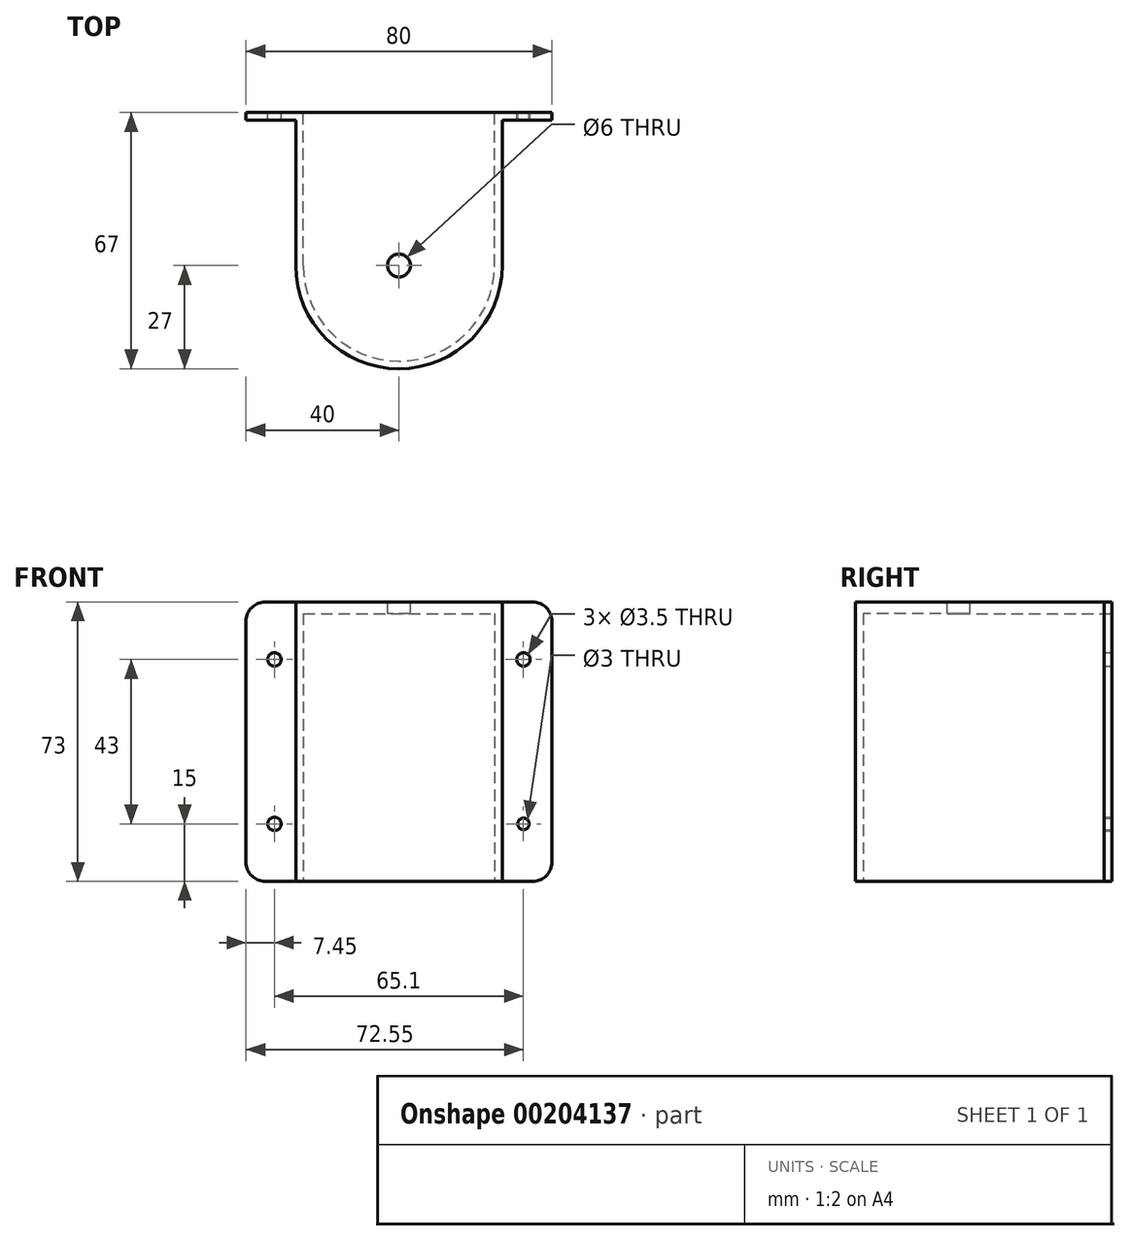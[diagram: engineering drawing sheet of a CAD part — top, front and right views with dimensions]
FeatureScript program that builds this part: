
annotation { "Feature Type Name" : "Feature", "Feature Type Description" : "" }
export const myFeature = defineFeature(function(context is Context, id is Id, definition is map)
    precondition{}
    {
        {
            var Q0;
            Q0=qCreatedBy(makeId("Top.planeOp"),FACE);
            var sketch = newSketch(context, id + "F0", { "sketchPlane" : qUnion([Q0])});
            skLineSegment(sketch, "E0", {"start": v(-25, 0) * mm, "end": v(25, 0) * mm, "construction": true});
            skArc(sketch, "E1", {"start": v(-25, 0) * mm, "mid": v(0, -25) * mm, "end": v(25, 0) * mm});
            skLineSegment(sketch, "E2", {"start": v(-25, 0) * mm, "end": v(-25, 40) * mm});
            skLineSegment(sketch, "E3", {"start": v(25, 0) * mm, "end": v(25, 40) * mm});
            skLineSegment(sketch, "E4", {"start": v(25, 40) * mm, "end": v(40, 40) * mm});
            skLineSegment(sketch, "E5", {"start": v(40, 40) * mm, "end": v(40, 38) * mm});
            skLineSegment(sketch, "E6", {"start": v(40, 38) * mm, "end": v(27, 38) * mm});
            skLineSegment(sketch, "E7", {"start": v(27, 38) * mm, "end": v(27, 0) * mm});
            skLineSegment(sketch, "E8", {"start": v(-25, 40) * mm, "end": v(-40, 40) * mm});
            skLineSegment(sketch, "E9", {"start": v(-40, 40) * mm, "end": v(-40, 38) * mm});
            skLineSegment(sketch, "E10", {"start": v(-40, 38) * mm, "end": v(-27, 38) * mm});
            skLineSegment(sketch, "E11", {"start": v(-27, 38) * mm, "end": v(-27, 0) * mm});
            skArc(sketch, "E12", {"start": v(-27, 0) * mm, "mid": v(0, -27) * mm, "end": v(27, 0) * mm});
            skSolve(sketch);
        }
        {
            var Q0;
            Q0=makeQuery(id+"F0.imprint","IMPRINT",FACE,{"disambiguationData":[TD([[makeQuery(id+"F0.imprint","IMPRINT",EDGE,{"derivedFrom":sQuery(id+"F0.wireOp",EDGE,"E1")}),-1.0]])]});
            extrude(context, id + "F1", {"entities" : qUnion([Q0]), "depth" : 70 * mm});
        }
        {
            var Q0;
            Q0=makeQuery(id+"F1.opExtrude","CAP_FACE",FACE,{"disambiguationData":[OSD([sQuery(id+"F0.wireOp",EDGE,"E1"),sQuery(id+"F0.wireOp",EDGE,"E2"),sQuery(id+"F0.wireOp",EDGE,"E3"),sQuery(id+"F0.wireOp",EDGE,"E4"),sQuery(id+"F0.wireOp",EDGE,"E5"),sQuery(id+"F0.wireOp",EDGE,"E6"),sQuery(id+"F0.wireOp",EDGE,"E7"),sQuery(id+"F0.wireOp",EDGE,"E8"),sQuery(id+"F0.wireOp",EDGE,"E9"),sQuery(id+"F0.wireOp",EDGE,"E10"),sQuery(id+"F0.wireOp",EDGE,"E11"),sQuery(id+"F0.wireOp",EDGE,"E12")])],"isStart":false});
            var sketch = newSketch(context, id + "F2", { "sketchPlane" : qUnion([Q0])});
            skLineSegment(sketch, "E13", {"start": v(-40, 40) * mm, "end": v(40, 40) * mm});
            skLineSegment(sketch, "E14", {"start": v(40, 40) * mm, "end": v(40, 38) * mm});
            skLineSegment(sketch, "E15", {"start": v(40, 38) * mm, "end": v(27, 38) * mm});
            skLineSegment(sketch, "E16", {"start": v(27, 38) * mm, "end": v(27, 0) * mm});
            skLineSegment(sketch, "E17", {"start": v(-40, 40) * mm, "end": v(-40, 38) * mm});
            skLineSegment(sketch, "E18", {"start": v(-40, 38) * mm, "end": v(-27, 38) * mm});
            skLineSegment(sketch, "E19", {"start": v(-27, 38) * mm, "end": v(-27, 0) * mm});
            skArc(sketch, "E20", {"start": v(-27, 0) * mm, "mid": v(0, -27) * mm, "end": v(27, 0) * mm});
            skSolve(sketch);
        }
        {
            var Q0;
            Q0 = qSketchRegion(id + "F2", true);
            extrude(context, id + "F3", {"entities" : qUnion([Q0]), "operationType" : NewBodyOperationType.ADD, "depth" : 3 * mm});
        }
        {
            var Q0;
            Q0=makeQuery(id+"F3.opExtrude","CAP_FACE",FACE,{"disambiguationData":[OSD([sQuery(id+"F2.wireOp",EDGE,"E13"),sQuery(id+"F2.wireOp",EDGE,"E14"),sQuery(id+"F2.wireOp",EDGE,"E15"),sQuery(id+"F2.wireOp",EDGE,"E16"),sQuery(id+"F2.wireOp",EDGE,"E17"),sQuery(id+"F2.wireOp",EDGE,"E18"),sQuery(id+"F2.wireOp",EDGE,"E19"),sQuery(id+"F2.wireOp",EDGE,"E20")])],"isStart":false});
            var sketch = newSketch(context, id + "F4", { "sketchPlane" : qUnion([Q0])});
            skCircle(sketch, "E21", {"center": v(0, 0) * mm, "radius": 3 * mm});
            skSolve(sketch);
        }
        {
            var Q0;
            Q0 = qSketchRegion(id + "F4", true);
            extrude(context, id + "F5", {"entities" : qUnion([Q0]), "operationType" : NewBodyOperationType.REMOVE, "endBound" : BoundingType.UP_TO_NEXT, "oppositeDirection" : true, "depth" : 3 * mm});
        }
        {
            var Q0;
            Q0=makeQuery(id+"F1.opExtrude","CAP_EDGE",EDGE,{"disambiguationData":[OSD([sQuery(id+"F0.wireOp",EDGE,"E5")])],"isStart":true});
            fillet(context, id + "F6", {"entities" : qUnion([Q0]), "radius" : 5 * mm, "tangentPropagation" : true, "allowEdgeOverflow" : false});
        }
        {
            var Q0;
            Q0=makeQuery(id+"F1.opExtrude","CAP_EDGE",EDGE,{"disambiguationData":[OSD([sQuery(id+"F0.wireOp",EDGE,"E9")])],"isStart":true});
            fillet(context, id + "F7", {"entities" : qUnion([Q0]), "radius" : 5 * mm, "tangentPropagation" : true, "allowEdgeOverflow" : false});
        }
        {
            var Q0;
            Q0=makeQuery(id+"F3.opExtrude","CAP_EDGE",EDGE,{"disambiguationData":[OSD([sQuery(id+"F2.wireOp",EDGE,"E17")])],"isStart":false});
            fillet(context, id + "F8", {"entities" : qUnion([Q0]), "radius" : 5 * mm, "tangentPropagation" : true, "allowEdgeOverflow" : false});
        }
        {
            var Q0;
            Q0=makeQuery(id+"F3.opExtrude","CAP_EDGE",EDGE,{"disambiguationData":[OSD([sQuery(id+"F2.wireOp",EDGE,"E14")])],"isStart":false});
            fillet(context, id + "F9", {"entities" : qUnion([Q0]), "radius" : 5 * mm, "tangentPropagation" : true, "allowEdgeOverflow" : false});
        }
        {
            var Q0;
            Q0=makeQuery(id+"F3.boolean.opBoolean","MERGE",FACE,{"derivedFrom":[makeQuery(id+"F1.opExtrude","SWEPT_FACE",FACE,{"disambiguationData":[OSD([sQuery(id+"F0.wireOp",EDGE,"E4")])]}),makeQuery(id+"F1.opExtrude","SWEPT_FACE",FACE,{"disambiguationData":[OSD([sQuery(id+"F0.wireOp",EDGE,"E8")])]}),makeQuery(id+"F3.opExtrude","SWEPT_FACE",FACE,{"disambiguationData":[OSD([sQuery(id+"F2.wireOp",EDGE,"E13")])]})]});
            var sketch = newSketch(context, id + "F10", { "sketchPlane" : qUnion([Q0])});
            skCircle(sketch, "E22", {"center": v(-32.55, 58) * mm, "radius": 1.75 * mm});
            skCircle(sketch, "E23", {"center": v(-32.55, 15) * mm, "radius": 1.5 * mm});
            skCircle(sketch, "E24", {"center": v(32.55, 15) * mm, "radius": 1.75 * mm});
            skCircle(sketch, "E25", {"center": v(32.55, 58) * mm, "radius": 1.75 * mm});
            skSolve(sketch);
        }
        {
            var Q0;
            Q0=makeQuery(id+"F10.imprint","IMPRINT",FACE,{"disambiguationData":[TD([[makeQuery(id+"F10.imprint","IMPRINT",EDGE,{"derivedFrom":sQuery(id+"F10.wireOp",EDGE,"E23")}),1.0]])]});
            var Q1;
            Q1=makeQuery(id+"F10.imprint","IMPRINT",FACE,{"disambiguationData":[TD([[makeQuery(id+"F10.imprint","IMPRINT",EDGE,{"derivedFrom":sQuery(id+"F10.wireOp",EDGE,"E22")}),1.0]])]});
            var Q2;
            Q2=makeQuery(id+"F10.imprint","IMPRINT",FACE,{"disambiguationData":[TD([[makeQuery(id+"F10.imprint","IMPRINT",EDGE,{"derivedFrom":sQuery(id+"F10.wireOp",EDGE,"E24")}),1.0]])]});
            var Q3;
            Q3=makeQuery(id+"F10.imprint","IMPRINT",FACE,{"disambiguationData":[TD([[makeQuery(id+"F10.imprint","IMPRINT",EDGE,{"derivedFrom":sQuery(id+"F10.wireOp",EDGE,"E25")}),1.0]])]});
            extrude(context, id + "F11", {"entities" : qUnion([Q0, Q1, Q2, Q3]), "operationType" : NewBodyOperationType.REMOVE, "oppositeDirection" : true, "depth" : 2 * mm});
        }
    });
